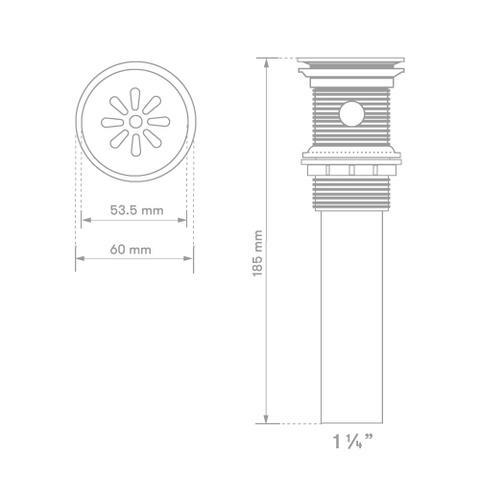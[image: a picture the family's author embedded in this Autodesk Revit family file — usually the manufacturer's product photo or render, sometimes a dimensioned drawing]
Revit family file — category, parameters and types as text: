
# Revit family: 01-1936-11 DESAGUE SENCILLO PLASTICO CON REBOSE
name_source: partatom
category: Aparatos sanitarios
revit_build: Autodesk Revit 2018 (Build: 20170223_1515(x64)
units: mm (PartAtom-declared; Revit-internal decimal feet)

## family parameters
Anfitrión = Cara
Compartido = No
Corte con vacíos al cargar = No
Cota de conector redondo = Diámetro de uso
Número OmniClass = 23.31.11.00
Punto de cálculo de habitación = No
Tipo de pieza = Normal

## types (1)
- 01-1936-11
    Acople = 31.8 mm  [stored 0.104331 ft]
    Alto = 185 mm  [stored 0.606955 ft]
    Caucho = Caucho
    Caucho espumoso blanco = Caucho Espumoso blanco
    Conexión AC = Sí
    Conexión AF = Sí
    Conexión de residuos = No
    Conexión de ventilación = No
    Descripción = Desague
    Diametro = 57.2 mm
    Elevación por defecto = 0 mm  [stored 0 ft]
    Fabricante = Gricol
    Imagen de tipo = <Ninguno>
    Link Ficha Tecnica = http://infotecnica.gricol.com
    Modelo = 01-1936-11
    Plastico - polipropileno + colorante gris = Plastico - polipropileno + colorante gris
    Plastico - polipropileno + colorante negro = Plastico - polipropileno + colorante Negro
    Plastico ABS Cromado = Plastico - ABS Cromado
    Product Name = DESAGUE SENCILLO PLASTICO CON REBOSE
    URL = https://www.gricol.com

note: [stored X ft] marks values corroborated as IEEE doubles in the binary element streams (Revit-internal decimal feet)

## geometry (parser evidence)
native form markers: Blend x2, Sweep x6
no freeform markers — native parametric forms only
